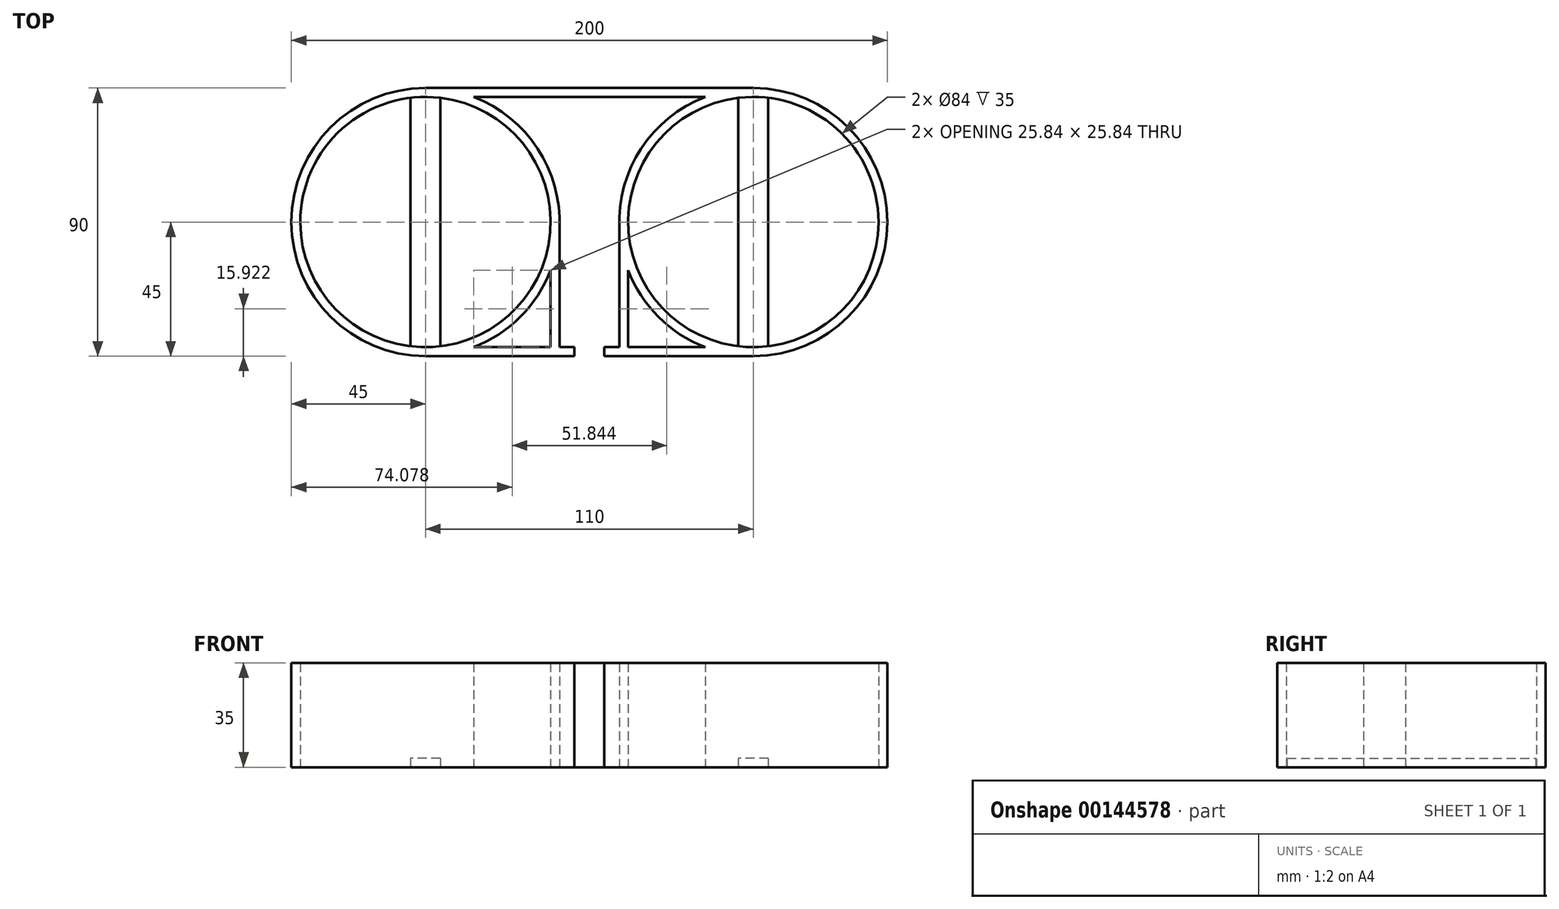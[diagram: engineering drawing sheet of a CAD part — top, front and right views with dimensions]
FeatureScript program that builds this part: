
annotation { "Feature Type Name" : "Feature", "Feature Type Description" : "" }
export const myFeature = defineFeature(function(context is Context, id is Id, definition is map)
    precondition{}
    {
        {
            var Q0;
            Q0=qCreatedBy(makeId("Top.planeOp"),FACE);
            var sketch = newSketch(context, id + "F0", { "sketchPlane" : qUnion([Q0])});
            skLineSegment(sketch, "E0", {"start": v(0, 0) * mm, "end": v(55, 0) * mm});
            skLineSegment(sketch, "E1", {"start": v(55, 0) * mm, "end": v(55, 90) * mm});
            skCircle(sketch, "E2", {"center": v(55, 45) * mm, "radius": 45 * mm});
            skLineSegment(sketch, "E3", {"start": v(0, 0) * mm, "end": v(0, 3) * mm});
            skLineSegment(sketch, "E4", {"start": v(0, 3) * mm, "end": v(55, 3) * mm});
            skCircle(sketch, "E5", {"center": v(55, 45) * mm, "radius": 42 * mm});
            skLineSegment(sketch, "E6", {"start": v(55, 45) * mm, "end": v(60, 45) * mm});
            skLineSegment(sketch, "E7", {"start": v(55, 45) * mm, "end": v(50, 45) * mm});
            skLineSegment(sketch, "E8", {"start": v(50, 45) * mm, "end": v(50, 86.7) * mm});
            skLineSegment(sketch, "E9", {"start": v(50, 45) * mm, "end": v(50, 3.3) * mm});
            skLineSegment(sketch, "E10", {"start": v(60, 45) * mm, "end": v(60, 86.7) * mm});
            skLineSegment(sketch, "E11", {"start": v(60, 45) * mm, "end": v(60, 3.3) * mm});
            skLineSegment(sketch, "E12", {"start": v(55, 90) * mm, "end": v(0, 90) * mm});
            skLineSegment(sketch, "E13", {"start": v(0, 90) * mm, "end": v(0, 87) * mm});
            skLineSegment(sketch, "E14", {"start": v(0, 87) * mm, "end": v(55, 87) * mm});
            skLineSegment(sketch, "E15", {"start": v(0, 3) * mm, "end": v(10, 3) * mm});
            skLineSegment(sketch, "E16", {"start": v(10, 3) * mm, "end": v(10, 0) * mm});
            skLineSegment(sketch, "E17", {"start": v(10, 3) * mm, "end": v(10, 43) * mm});
            skPoint(sketch, "E17.endSnap0", {"position": v(10, 1.5) * mm});
            skLineSegment(sketch, "E18", {"start": v(10, 3) * mm, "end": v(13, 3) * mm});
            skLineSegment(sketch, "E19", {"start": v(13, 3) * mm, "end": v(13, 43) * mm});
            skLineSegment(sketch, "E20", {"start": v(10, 43) * mm, "end": v(13, 43) * mm});
            skLineSegment(sketch, "E21", {"start": v(5, 3) * mm, "end": v(5, 0) * mm});
            skSolve(sketch);
        }
        {
            var Q0;
            {var subQ0=sQuery(id+"F0.wireOp",EDGE,"E16");Q0=makeQuery(id+"F0.imprint","IMPRINT",FACE,{"disambiguationData":[TD([[makeQuery(id+"F0.imprint","IMPRINT",EDGE,{"derivedFrom":subQ0}),-1.0]])]});}
            var Q1;
            {var subQ0=sQuery(id+"F0.wireOp",EDGE,"E16");Q1=makeQuery(id+"F0.imprint","IMPRINT",FACE,{"disambiguationData":[TD([[makeQuery(id+"F0.imprint","IMPRINT",EDGE,{"derivedFrom":subQ0}),1.0]])]});}
            var Q2;
            {var subQ4=sQuery(id+"F0.wireOp",EDGE,"E17");Q2=makeQuery(id+"F0.imprint","IMPRINT",FACE,{"disambiguationData":[TD([[makeQuery(id+"F0.imprint","IMPRINT",EDGE,{"derivedFrom":subQ4}),-1.0]])]});}
            var Q3;
            {var subQ0=sQuery(id+"F0.wireOp",EDGE,"E2");var subQ3=sQuery(id+"F0.wireOp",EDGE,"E4");var subQ5=makeQuery(id+"F0.imprint","INTERSECT",VERTEX,{"derivedFrom":[subQ0,subQ3]});Q3=makeQuery(id+"F0.imprint","IMPRINT",FACE,{"disambiguationData":[TD([[makeQuery(id+"F0.imprint","IMPRINT",EDGE,{"disambiguationData":[TD([[subQ5,-1.0]])],"derivedFrom":subQ0}),1.0]])]});}
            var Q4;
            {var subQ2=sQuery(id+"F0.wireOp",EDGE,"E14");var subQ5=sQuery(id+"F0.wireOp",EDGE,"E2");var subQ6=makeQuery(id+"F0.imprint","INTERSECT",VERTEX,{"derivedFrom":[subQ5,subQ2]});Q4=makeQuery(id+"F0.imprint","IMPRINT",FACE,{"disambiguationData":[TD([[makeQuery(id+"F0.imprint","IMPRINT",EDGE,{"disambiguationData":[TD([[subQ6,-1.0]])],"derivedFrom":subQ5}),1.0]])]});}
            var Q5;
            {var subQ4=sQuery(id+"F0.wireOp",EDGE,"E5");var subQ5=makeQuery(id+"F0.imprint","INTERSECT",VERTEX,{"derivedFrom":[subQ4,sQuery(id+"F0.wireOp",EDGE,"E10")]});Q5=makeQuery(id+"F0.imprint","IMPRINT",FACE,{"disambiguationData":[TD([[makeQuery(id+"F0.imprint","IMPRINT",EDGE,{"disambiguationData":[TD([[subQ5,1.0]])],"derivedFrom":subQ4}),-1.0]])]});}
            var Q6;
            {var subQ0=sQuery(id+"F0.wireOp",EDGE,"E2");var subQ3=sQuery(id+"F0.wireOp",EDGE,"E14");var subQ5=makeQuery(id+"F0.imprint","INTERSECT",VERTEX,{"derivedFrom":[subQ0,subQ3]});Q6=makeQuery(id+"F0.imprint","IMPRINT",FACE,{"disambiguationData":[TD([[makeQuery(id+"F0.imprint","IMPRINT",EDGE,{"disambiguationData":[TD([[subQ5,1.0]])],"derivedFrom":subQ0}),1.0]])]});}
            var Q7;
            {var subQ0=sQuery(id+"F0.wireOp",EDGE,"E12");Q7=makeQuery(id+"F0.imprint","IMPRINT",FACE,{"disambiguationData":[TD([[makeQuery(id+"F0.imprint","IMPRINT",EDGE,{"derivedFrom":subQ0}),1.0]])]});}
            var Q8;
            {var subQ0=sQuery(id+"F0.wireOp",EDGE,"E20");var subQ1=sQuery(id+"F0.wireOp",EDGE,"E2");var subQ2=makeQuery(id+"F0.imprint","INTERSECT",VERTEX,{"derivedFrom":[subQ1,subQ0]});Q8=makeQuery(id+"F0.imprint","IMPRINT",FACE,{"disambiguationData":[TD([[makeQuery(id+"F0.imprint","IMPRINT",EDGE,{"disambiguationData":[TD([[subQ2,-1.0]])],"derivedFrom":subQ1}),1.0]])]});}
            extrude(context, id + "F1", {"entities" : qUnion([Q0, Q1, Q2, Q3, Q4, Q5, Q6, Q7, Q8]), "depth" : 35 * mm});
        }
        {
            var Q0;
            {var subQ0=sQuery(id+"F0.wireOp",EDGE,"E7");Q0=makeQuery(id+"F0.imprint","IMPRINT",FACE,{"disambiguationData":[TD([[makeQuery(id+"F0.imprint","IMPRINT",EDGE,{"derivedFrom":subQ0}),-1.0]])]});}
            var Q1;
            {var subQ0=sQuery(id+"F0.wireOp",EDGE,"E6");Q1=makeQuery(id+"F0.imprint","IMPRINT",FACE,{"disambiguationData":[TD([[makeQuery(id+"F0.imprint","IMPRINT",EDGE,{"derivedFrom":subQ0}),1.0]])]});}
            var Q2;
            {var subQ3=sQuery(id+"F0.wireOp",EDGE,"E7");Q2=makeQuery(id+"F0.imprint","IMPRINT",FACE,{"disambiguationData":[TD([[makeQuery(id+"F0.imprint","IMPRINT",EDGE,{"derivedFrom":subQ3}),1.0]])]});}
            var Q3;
            {var subQ3=sQuery(id+"F0.wireOp",EDGE,"E6");Q3=makeQuery(id+"F0.imprint","IMPRINT",FACE,{"disambiguationData":[TD([[makeQuery(id+"F0.imprint","IMPRINT",EDGE,{"derivedFrom":subQ3}),-1.0]])]});}
            extrude(context, id + "F2", {"entities" : qUnion([Q0, Q1, Q2, Q3]), "operationType" : NewBodyOperationType.ADD, "depth" : 3 * mm});
        }
        {
            var Q0;
            Q0=makeQuery(id+"F1.opExtrude","SWEPT_BODY",BODY,{"disambiguationData":[OSD([sQuery(id+"F0.wireOp",EDGE,"E0"),sQuery(id+"F0.wireOp",EDGE,"E2"),sQuery(id+"F0.wireOp",EDGE,"E4"),sQuery(id+"F0.wireOp",EDGE,"E5"),sQuery(id+"F0.wireOp",EDGE,"E12"),sQuery(id+"F0.wireOp",EDGE,"E13"),sQuery(id+"F0.wireOp",EDGE,"E14"),sQuery(id+"F0.wireOp",EDGE,"E15"),sQuery(id+"F0.wireOp",EDGE,"E17"),sQuery(id+"F0.wireOp",EDGE,"E19"),sQuery(id+"F0.wireOp",EDGE,"E20"),sQuery(id+"F0.wireOp",EDGE,"E21")])]});
            var Q1;
            Q1=qCreatedBy(makeId("Right.planeOp"),FACE);
            mirror(context, id + "F3", {"operationType" : NewBodyOperationType.ADD, "entities" : qUnion([Q0]), "mirrorPlane" : qUnion([Q1])});
        }
    });
